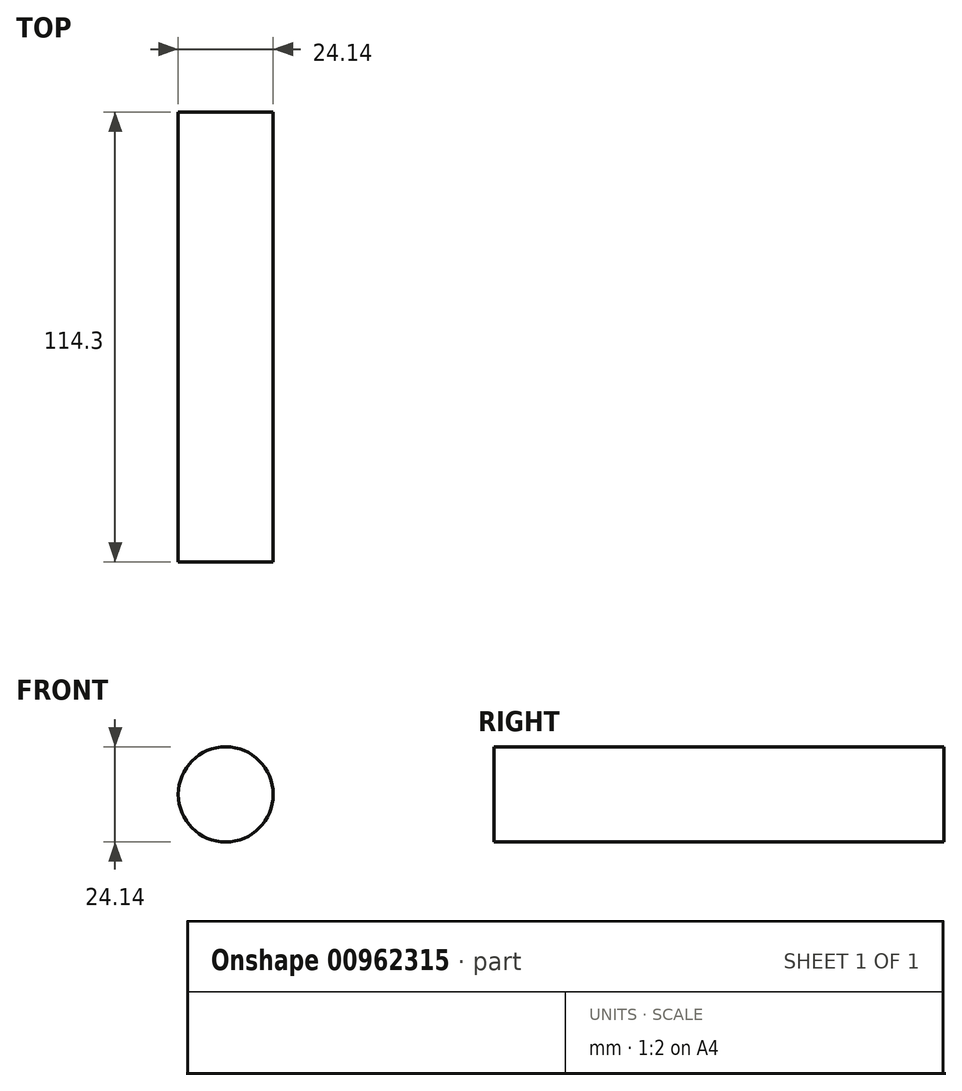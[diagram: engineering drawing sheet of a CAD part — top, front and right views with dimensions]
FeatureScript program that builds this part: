
annotation { "Feature Type Name" : "Feature", "Feature Type Description" : "" }
export const myFeature = defineFeature(function(context is Context, id is Id, definition is map)
    precondition{}
    {
        {
            var Q0;
            Q0=qCreatedBy(makeId("Front.planeOp"),FACE);
            var sketch = newSketch(context, id + "F0", { "sketchPlane" : qUnion([Q0])});
            skCircle(sketch, "E0", {"center": v(0, 0) * mm, "radius": 12.07 * mm});
            skSolve(sketch);
        }
        {
            var Q0;
            Q0=makeQuery(id+"F0.imprint","IMPRINT",FACE,{"disambiguationData":[TD([[makeQuery(id+"F0.imprint","IMPRINT",EDGE,{"derivedFrom":sQuery(id+"F0.wireOp",EDGE,"E0")}),1.0]])]});
            extrude(context, id + "F1", {"entities" : qUnion([Q0]), "depth" : 114.3 * mm, "offsetDistance" : 25.4 * mm});
        }
    });
